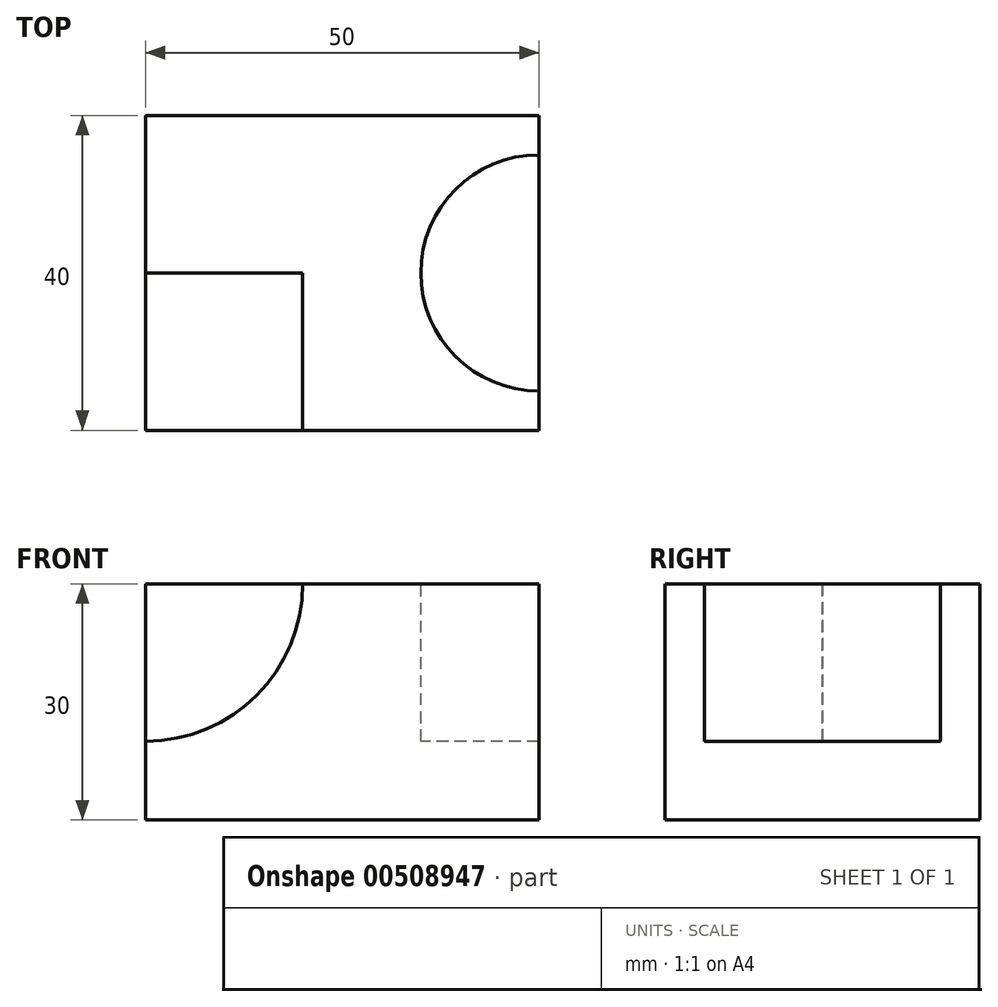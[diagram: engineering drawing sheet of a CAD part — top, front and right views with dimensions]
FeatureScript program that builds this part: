
annotation { "Feature Type Name" : "Feature", "Feature Type Description" : "" }
export const myFeature = defineFeature(function(context is Context, id is Id, definition is map)
    precondition{}
    {
        {
            var Q0;
            Q0=qCreatedBy(makeId("Top.planeOp"),FACE);
            var sketch = newSketch(context, id + "F0", { "sketchPlane" : qUnion([Q0])});
            skLineSegment(sketch, "E0.bottom", {"start": v(-25, 20) * mm, "end": v(25, 20) * mm});
            skLineSegment(sketch, "E0.top", {"start": v(-25, -20) * mm, "end": v(25, -20) * mm});
            skLineSegment(sketch, "E0.left", {"start": v(-25, 20) * mm, "end": v(-25, -20) * mm});
            skLineSegment(sketch, "E0.right", {"start": v(25, 20) * mm, "end": v(25, -20) * mm});
            skPoint(sketch, "E0.middle", {"position": v(0, 0) * mm});
            skSolve(sketch);
        }
        {
            var Q0;
            Q0 = qSketchRegion(id + "F0", true);
            extrude(context, id + "F1", {"entities" : qUnion([Q0]), "depth" : 30 * mm});
        }
        {
            var Q0;
            Q0=makeQuery(id+"F1.opExtrude","SWEPT_FACE",FACE,{"disambiguationData":[OSD([sQuery(id+"F0.wireOp",EDGE,"E0.top")])]});
            var sketch = newSketch(context, id + "F2", { "sketchPlane" : qUnion([Q0])});
            skCircle(sketch, "E1", {"center": v(-25, 30) * mm, "radius": 20 * mm});
            skSolve(sketch);
        }
        {
            var Q0;
            Q0 = qSketchRegion(id + "F2", true);
            extrude(context, id + "F3", {"entities" : qUnion([Q0]), "operationType" : NewBodyOperationType.REMOVE, "oppositeDirection" : true, "depth" : 20 * mm});
        }
        {
            var Q0;
            Q0=makeQuery(id+"F1.opExtrude","CAP_FACE",FACE,{"disambiguationData":[OSD([sQuery(id+"F0.wireOp",EDGE,"E0.bottom"),sQuery(id+"F0.wireOp",EDGE,"E0.top"),sQuery(id+"F0.wireOp",EDGE,"E0.left"),sQuery(id+"F0.wireOp",EDGE,"E0.right")])],"isStart":false});
            var sketch = newSketch(context, id + "F4", { "sketchPlane" : qUnion([Q0])});
            skCircle(sketch, "E2", {"center": v(25, 0) * mm, "radius": 15 * mm});
            skSolve(sketch);
        }
        {
            var Q0;
            Q0 = qSketchRegion(id + "F4", true);
            extrude(context, id + "F5", {"entities" : qUnion([Q0]), "operationType" : NewBodyOperationType.REMOVE, "oppositeDirection" : true, "depth" : 20 * mm});
        }
    });
